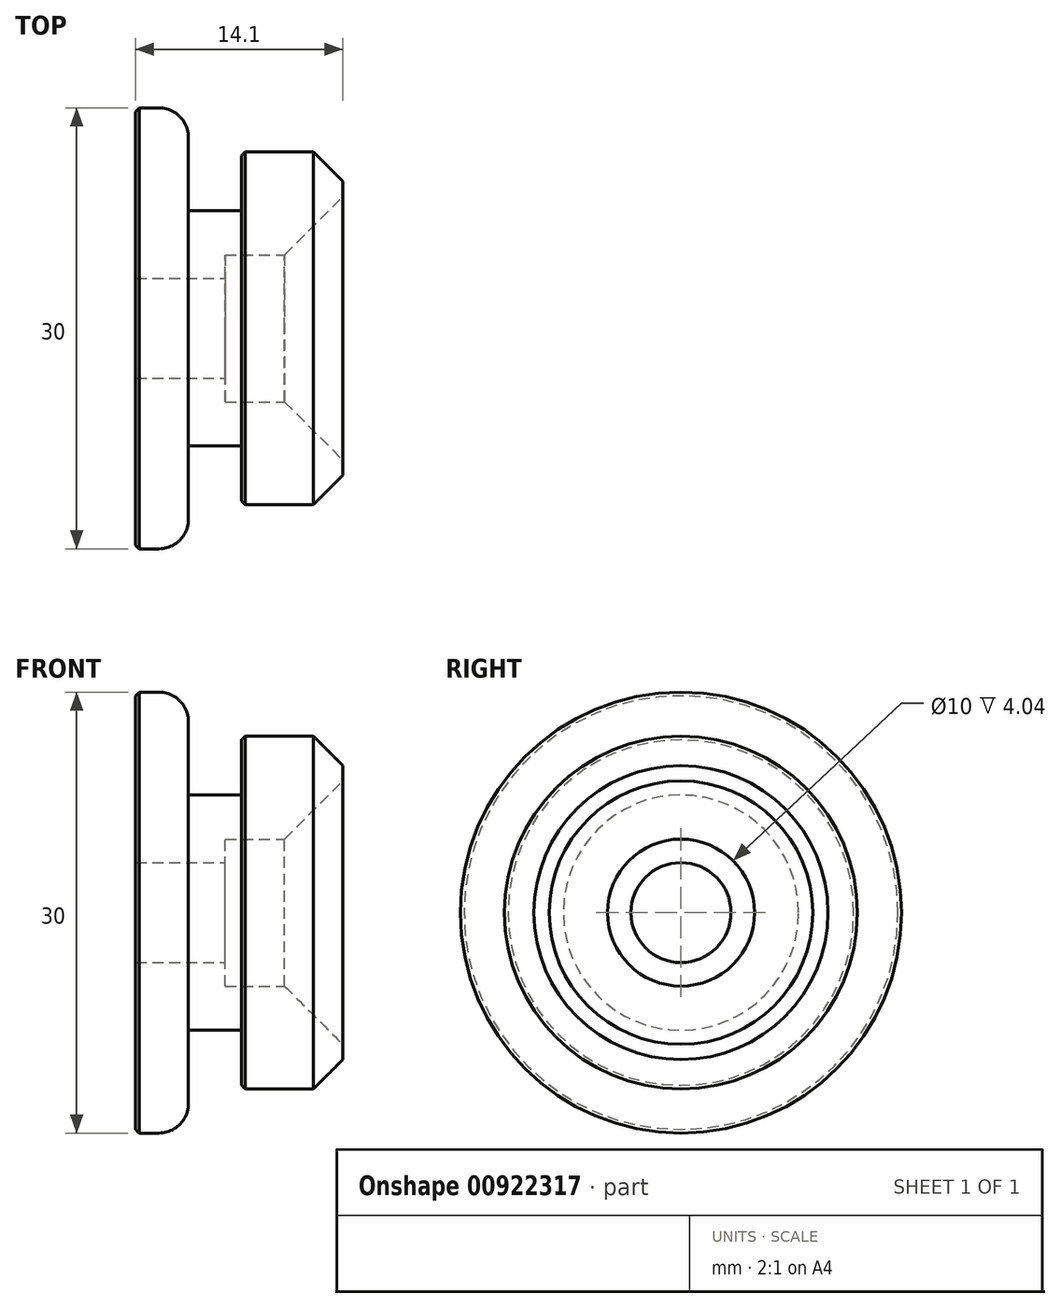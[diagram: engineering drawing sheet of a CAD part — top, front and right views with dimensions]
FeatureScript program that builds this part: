
annotation { "Feature Type Name" : "Feature", "Feature Type Description" : "" }
export const myFeature = defineFeature(function(context is Context, id is Id, definition is map)
    precondition{}
    {
        {
            var Q0;
            Q0=qCreatedBy(makeId("Right.planeOp"),FACE);
            var sketch = newSketch(context, id + "F0", { "sketchPlane" : qUnion([Q0])});
            skCircle(sketch, "E0", {"center": v(0, 0) * mm, "radius": 15 * mm});
            skSolve(sketch);
        }
        {
            var Q0;
            Q0=makeQuery(id+"F0.imprint","IMPRINT",FACE,{"disambiguationData":[TD([[makeQuery(id+"F0.imprint","IMPRINT",EDGE,{"derivedFrom":sQuery(id+"F0.wireOp",EDGE,"E0")}),1.0]])]});
            extrude(context, id + "F1", {"entities" : qUnion([Q0]), "depth" : 3.6 * mm, "offsetDistance" : 25 * mm});
        }
        {
            var Q0;
            Q0=makeQuery(id+"F1.opExtrude","CAP_FACE",FACE,{"disambiguationData":[OSD([sQuery(id+"F0.wireOp",EDGE,"E0")])],"isStart":false});
            var sketch = newSketch(context, id + "F2", { "sketchPlane" : qUnion([Q0])});
            skCircle(sketch, "E1", {"center": v(0, 0) * mm, "radius": 12 * mm});
            skSolve(sketch);
        }
        {
            var Q0;
            Q0=makeQuery(id+"F2.imprint","IMPRINT",FACE,{"disambiguationData":[TD([[makeQuery(id+"F2.imprint","IMPRINT",EDGE,{"derivedFrom":sQuery(id+"F2.wireOp",EDGE,"E1")}),1.0]])]});
            extrude(context, id + "F3", {"entities" : qUnion([Q0]), "operationType" : NewBodyOperationType.ADD, "depth" : 10.5 * mm, "offsetDistance" : 25 * mm});
        }
        {
            var Q0;
            Q0=makeQuery(id+"F3.opExtrude","CAP_FACE",FACE,{"disambiguationData":[OSD([sQuery(id+"F2.wireOp",EDGE,"E1")])],"isStart":false});
            var sketch = newSketch(context, id + "F4", { "sketchPlane" : qUnion([Q0])});
            skPoint(sketch, "E2", {"position": v(0, 0) * mm});
            skSolve(sketch);
        }
        {
            var Q0;
            Q0=sQuery(id+"F4.wireOp",VERTEX,"E2");
            var Q1;
            Q1=makeQuery(id+"F1.opExtrude","SWEPT_BODY",BODY,{"disambiguationData":[OSD([sQuery(id+"F0.wireOp",EDGE,"E0")])]});
            hole(context, id + "F5", {"style" : HoleStyle.C_SINK, "endStyle" : HoleEndStyle.THROUGH, "standardTappedOrClearance" : lookupTablePath({ "standard" : "ISO", "engagement" : "75%", "pitch" : "1.25 mm", "size" : "M8", "type" : "Tapped" }), "standardBlindInLast" : lookupTablePath({ "standard" : "ISO", "fit" : "Normal", "engagement" : "75%", "pitch" : "1.25 mm", "size" : "M8", "type" : "Clearance & tapped" }), "holeDiameter" : 6.8 * mm, "cSinkDiameter" : 17.92 * mm, "cSinkAngle" : 90 * degree, "majorDiameter" : 8 * mm, "showTappedDepth" : true, "isTappedThrough" : true, "tappedDepth" : 12 * mm, "tapClearance" : 3, "locations" : qUnion([Q0]), "scope" : qUnion([Q1])});
        }
        {
            var Q0;
            Q0=qCreatedBy(makeId("Front.planeOp"),FACE);
            var sketch = newSketch(context, id + "F6", { "sketchPlane" : qUnion([Q0])});
            skLineSegment(sketch, "E3", {"start": v(-9.65, 0) * mm, "end": v(26.76, 0) * mm, "construction": true});
            skLineSegment(sketch, "E4.bottom", {"start": v(3.6, 13) * mm, "end": v(7.2, 13) * mm});
            skLineSegment(sketch, "E4.top", {"start": v(3.6, 8) * mm, "end": v(7.2, 8) * mm});
            skLineSegment(sketch, "E4.left", {"start": v(3.6, 13) * mm, "end": v(3.6, 8) * mm});
            skLineSegment(sketch, "E4.right", {"start": v(7.2, 13) * mm, "end": v(7.2, 8) * mm});
            skSolve(sketch);
        }
        {
            var Q0;
            Q0=makeQuery(id+"F6.imprint","IMPRINT",FACE,{"disambiguationData":[TD([[makeQuery(id+"F6.imprint","IMPRINT",EDGE,{"derivedFrom":sQuery(id+"F6.wireOp",EDGE,"E4.bottom")}),-1.0]])]});
            var Q1;
            Q1=sQuery(id+"F6.wireOp",EDGE,"E3");
            revolve(context, id + "F7", {"operationType" : NewBodyOperationType.REMOVE, "surfaceOperationType" : NewSurfaceOperationType.NEW, "entities" : qUnion([Q0]), "axis" : qUnion([Q1]), "revolveType" : RevolveType.FULL, "oppositeDirection" : true});
        }
        {
            var Q0;
            Q0=makeQuery(id+"F1.opExtrude","CAP_EDGE",EDGE,{"disambiguationData":[OSD([sQuery(id+"F0.wireOp",EDGE,"E0")])],"isStart":true});
            var Q1;
            Q1=makeQuery(id+"F7.boolean.opBoolean","INTERSECT",EDGE,{"derivedFrom":[makeQuery(id+"F3.opExtrude","SWEPT_FACE",FACE,{"disambiguationData":[OSD([sQuery(id+"F2.wireOp",EDGE,"E1")])]}),makeQuery(id+"F7.opRevolve","SWEPT_FACE",FACE,{"disambiguationData":[OSD([sQuery(id+"F6.wireOp",EDGE,"E4.right")])]})]});
            chamfer(context, id + "F8", {"entities" : qUnion([Q0, Q1]), "width" : 0.25 * mm, "tangentPropagation" : true});
        }
        {
            var Q0;
            Q0=makeQuery(id+"F1.opExtrude","CAP_EDGE",EDGE,{"disambiguationData":[OSD([sQuery(id+"F0.wireOp",EDGE,"E0")])],"isStart":false});
            fillet(context, id + "F9", {"entities" : qUnion([Q0]), "radius" : 2 * mm, "tangentPropagation" : true, "allowEdgeOverflow" : false});
        }
        {
            var Q0;
            Q0=makeQuery(id+"F3.opExtrude","CAP_EDGE",EDGE,{"disambiguationData":[OSD([sQuery(id+"F2.wireOp",EDGE,"E1")])],"isStart":false});
            chamfer(context, id + "F10", {"entities" : qUnion([Q0]), "width" : 2 * mm, "tangentPropagation" : true});
        }
        {
            var Q0;
            Q0=makeQuery(id+"F3.opExtrude","CAP_FACE",FACE,{"disambiguationData":[OSD([sQuery(id+"F2.wireOp",EDGE,"E1")])],"isStart":false});
            var sketch = newSketch(context, id + "F11", { "sketchPlane" : qUnion([Q0])});
            skCircle(sketch, "E5", {"center": v(0, 0) * mm, "radius": 5 * mm});
            skSolve(sketch);
        }
        {
            var Q0;
            Q0=makeQuery(id+"F11.imprint","IMPRINT",FACE,{"disambiguationData":[TD([[makeQuery(id+"F11.imprint","IMPRINT",EDGE,{"derivedFrom":sQuery(id+"F11.wireOp",EDGE,"E5")}),1.0]])]});
            extrude(context, id + "F12", {"entities" : qUnion([Q0]), "operationType" : NewBodyOperationType.REMOVE, "oppositeDirection" : true, "depth" : 8 * mm, "offsetDistance" : 25 * mm});
        }
    });
